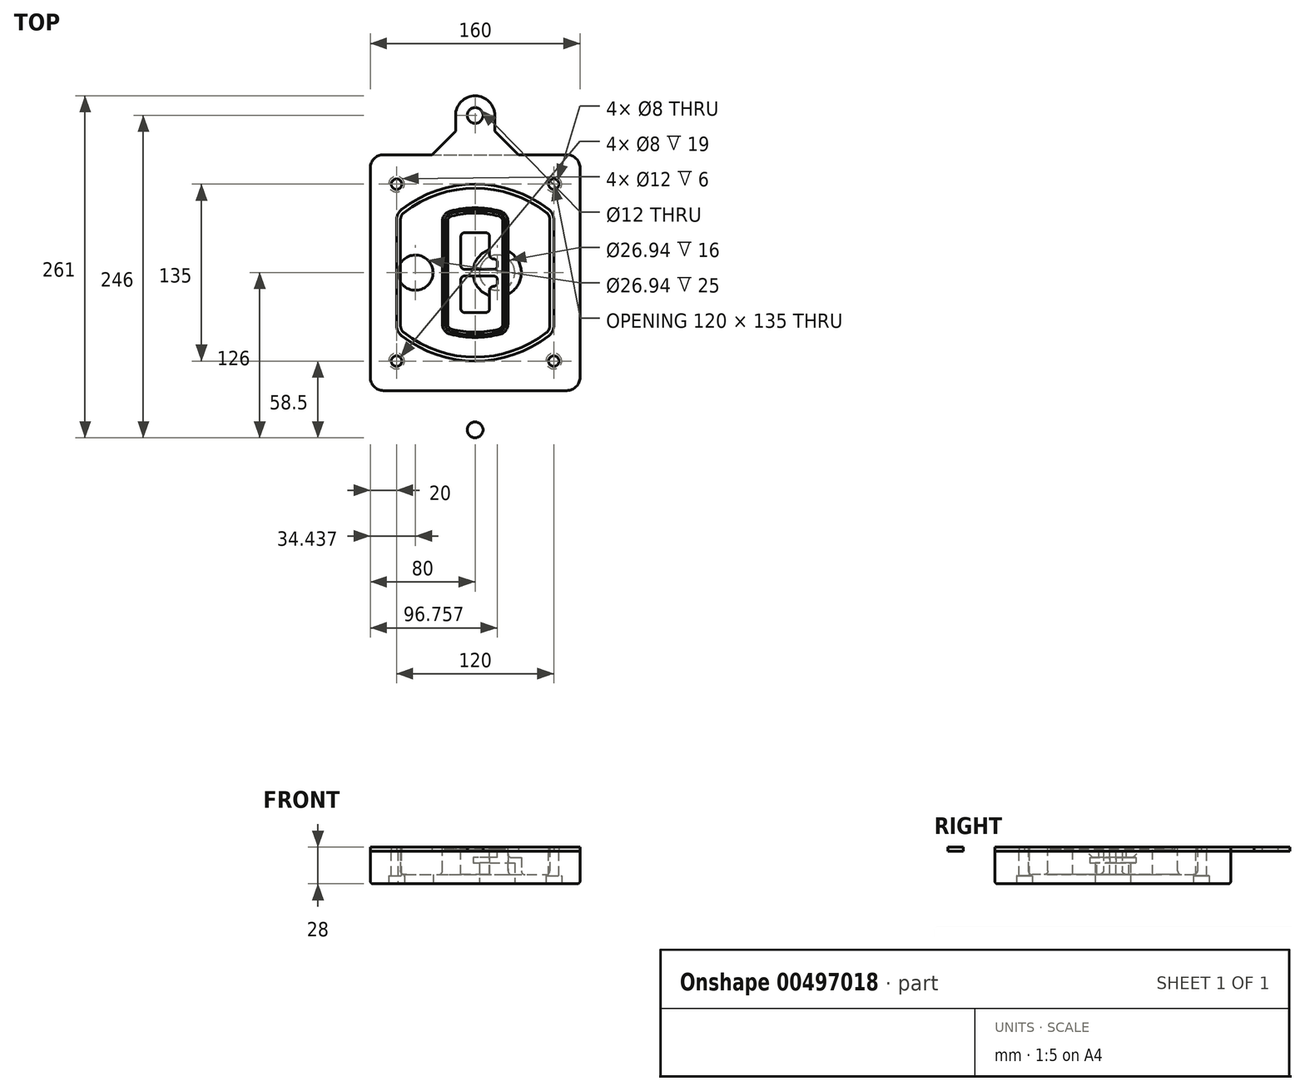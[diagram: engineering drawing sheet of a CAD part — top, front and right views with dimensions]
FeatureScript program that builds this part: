
annotation { "Feature Type Name" : "Feature", "Feature Type Description" : "" }
export const myFeature = defineFeature(function(context is Context, id is Id, definition is map)
    precondition{}
    {
        {
            var Q0;
            Q0=qCreatedBy(makeId("Top.planeOp"),FACE);
            var sketch = newSketch(context, id + "F0", { "sketchPlane" : qUnion([Q0])});
            skPoint(sketch, "E0.rect.middle", {"position": v(0, 0) * mm});
            skLineSegment(sketch, "E1.bottom", {"start": v(-70, -90) * mm, "end": v(70, -90) * mm});
            skLineSegment(sketch, "E1.top", {"start": v(-70, 90) * mm, "end": v(70, 90) * mm});
            skLineSegment(sketch, "E1.left", {"start": v(-80, -80) * mm, "end": v(-80, 80) * mm});
            skLineSegment(sketch, "E1.right", {"start": v(80, -80) * mm, "end": v(80, 80) * mm});
            skLineSegment(sketch, "E2", {"start": v(-80, 90) * mm, "end": v(80, -90) * mm, "construction": true});
            skLineSegment(sketch, "E3", {"start": v(80, 90) * mm, "end": v(-80, -90) * mm, "construction": true});
            skCircle(sketch, "E4", {"center": v(-60, 67.5) * mm, "radius": 4 * mm});
            skCircle(sketch, "E5", {"center": v(60, 67.5) * mm, "radius": 4 * mm});
            skCircle(sketch, "E6", {"center": v(60, -67.5) * mm, "radius": 4 * mm});
            skCircle(sketch, "E7", {"center": v(-60, -67.5) * mm, "radius": 4 * mm});
            skLineSegment(sketch, "E8", {"start": v(-60, 67.5) * mm, "end": v(60, 67.5) * mm, "construction": true});
            skLineSegment(sketch, "E9", {"start": v(60, 67.5) * mm, "end": v(60, -67.5) * mm, "construction": true});
            skLineSegment(sketch, "E10", {"start": v(60, -67.5) * mm, "end": v(-60, -67.5) * mm, "construction": true});
            skLineSegment(sketch, "E11", {"start": v(-60, -67.5) * mm, "end": v(-60, 67.5) * mm, "construction": true});
            skLineSegment(sketch, "E12", {"start": v(-60, 40.3) * mm, "end": v(-60, -40.3) * mm});
            skLineSegment(sketch, "E13", {"start": v(60, 40.3) * mm, "end": v(60, -40.3) * mm});
            skArc(sketch, "E14", {"start": v(56.15, 48.18) * mm, "mid": v(0, 67.5) * mm, "end": v(-56.15, 48.18) * mm});
            skArc(sketch, "E15", {"start": v(-56.15, -48.18) * mm, "mid": v(0, -67.5) * mm, "end": v(56.15, -48.18) * mm});
            skLineSegment(sketch, "E16", {"start": v(-60, 0) * mm, "end": v(60, 0) * mm, "construction": true});
            skPoint(sketch, "E17.visualSharp", {"position": v(-60, -45) * mm});
            skArc(sketch, "E17.filletArc", {"start": v(-60, -40.3) * mm, "mid": v(-58.99, -44.68) * mm, "end": v(-56.15, -48.18) * mm});
            skPoint(sketch, "E18.visualSharp", {"position": v(-60, 45) * mm});
            skArc(sketch, "E18.filletArc", {"start": v(-56.15, 48.18) * mm, "mid": v(-58.99, 44.68) * mm, "end": v(-60, 40.3) * mm});
            skPoint(sketch, "E19.visualSharp", {"position": v(60, 45) * mm});
            skArc(sketch, "E19.filletArc", {"start": v(60, 40.3) * mm, "mid": v(58.99, 44.68) * mm, "end": v(56.15, 48.18) * mm});
            skPoint(sketch, "E20.visualSharp", {"position": v(60, -45) * mm});
            skArc(sketch, "E20.filletArc", {"start": v(56.15, -48.18) * mm, "mid": v(58.99, -44.68) * mm, "end": v(60, -40.3) * mm});
            skPoint(sketch, "E21.visualSharp", {"position": v(-80, 90) * mm});
            skArc(sketch, "E21.filletArc", {"start": v(-70, 90) * mm, "mid": v(-77.07, 87.07) * mm, "end": v(-80, 80) * mm});
            skPoint(sketch, "E22.visualSharp", {"position": v(80, 90) * mm});
            skArc(sketch, "E22.filletArc", {"start": v(80, 80) * mm, "mid": v(77.07, 87.07) * mm, "end": v(70, 90) * mm});
            skPoint(sketch, "E23.visualSharp", {"position": v(80, -90) * mm});
            skArc(sketch, "E23.filletArc", {"start": v(70, -90) * mm, "mid": v(77.07, -87.07) * mm, "end": v(80, -80) * mm});
            skPoint(sketch, "E24.visualSharp", {"position": v(-80, -90) * mm});
            skArc(sketch, "E24.filletArc", {"start": v(-80, -80) * mm, "mid": v(-77.07, -87.07) * mm, "end": v(-70, -90) * mm});
            skArc(sketch, "E25.0", {"start": v(57, 40.3) * mm, "mid": v(56.3, 43.36) * mm, "end": v(54.3, 45.81) * mm});
            skLineSegment(sketch, "E25.1", {"start": v(57, 40.3) * mm, "end": v(57, -40.3) * mm});
            skArc(sketch, "E25.2", {"start": v(54.3, -45.81) * mm, "mid": v(56.3, -43.36) * mm, "end": v(57, -40.3) * mm});
            skArc(sketch, "E25.3", {"start": v(-54.3, -45.81) * mm, "mid": v(0, -64.5) * mm, "end": v(54.3, -45.81) * mm});
            skArc(sketch, "E25.4", {"start": v(-57, -40.3) * mm, "mid": v(-56.3, -43.36) * mm, "end": v(-54.3, -45.81) * mm});
            skArc(sketch, "E25.5", {"start": v(54.3, 45.81) * mm, "mid": v(0, 64.5) * mm, "end": v(-54.3, 45.81) * mm});
            skLineSegment(sketch, "E25.6", {"start": v(-57, 40.3) * mm, "end": v(-57, -40.3) * mm});
            skArc(sketch, "E25.7", {"start": v(-54.3, 45.81) * mm, "mid": v(-56.3, 43.36) * mm, "end": v(-57, 40.3) * mm});
            skArc(sketch, "E26.0", {"start": v(-58.62, 51.33) * mm, "mid": v(-62.58, 46.43) * mm, "end": v(-64, 40.3) * mm});
            skArc(sketch, "E26.1", {"start": v(58.62, 51.33) * mm, "mid": v(0, 71.5) * mm, "end": v(-58.62, 51.33) * mm});
            skArc(sketch, "E26.2", {"start": v(64, 40.3) * mm, "mid": v(62.58, 46.43) * mm, "end": v(58.62, 51.33) * mm});
            skLineSegment(sketch, "E26.3", {"start": v(64, 40.3) * mm, "end": v(64, -40.3) * mm});
            skArc(sketch, "E26.4", {"start": v(58.62, -51.33) * mm, "mid": v(62.58, -46.43) * mm, "end": v(64, -40.3) * mm});
            skLineSegment(sketch, "E26.5", {"start": v(-64, 40.3) * mm, "end": v(-64, -40.3) * mm});
            skArc(sketch, "E26.6", {"start": v(-58.62, -51.33) * mm, "mid": v(0, -71.5) * mm, "end": v(58.62, -51.33) * mm});
            skArc(sketch, "E26.7", {"start": v(-64, -40.3) * mm, "mid": v(-62.58, -46.43) * mm, "end": v(-58.62, -51.33) * mm});
            skSolve(sketch);
        }
        {
            var Q0;
            Q0=makeQuery(id+"F0.imprint","IMPRINT",FACE,{"disambiguationData":[TD([[makeQuery(id+"F0.imprint","IMPRINT",EDGE,{"derivedFrom":sQuery(id+"F0.wireOp",EDGE,"E1.bottom")}),1.0]])]});
            var Q1;
            Q1=makeQuery(id+"F0.imprint","IMPRINT",FACE,{"disambiguationData":[TD([[makeQuery(id+"F0.imprint","IMPRINT",EDGE,{"derivedFrom":sQuery(id+"F0.wireOp",EDGE,"E12")}),1.0]])]});
            var Q2;
            Q2=makeQuery(id+"F0.imprint","IMPRINT",FACE,{"disambiguationData":[TD([[makeQuery(id+"F0.imprint","IMPRINT",EDGE,{"derivedFrom":sQuery(id+"F0.wireOp",EDGE,"E25.0")}),1.0]])]});
            var Q3;
            Q3=makeQuery(id+"F0.imprint","IMPRINT",FACE,{"disambiguationData":[TD([[makeQuery(id+"F0.imprint","IMPRINT",EDGE,{"derivedFrom":sQuery(id+"F0.wireOp",EDGE,"E12")}),-1.0]])]});
            extrude(context, id + "F1", {"entities" : qUnion([Q0, Q1, Q2, Q3]), "oppositeDirection" : true, "depth" : 25 * mm});
        }
        {
            var Q0;
            Q0=makeQuery(id+"F0.imprint","IMPRINT",FACE,{"disambiguationData":[TD([[makeQuery(id+"F0.imprint","IMPRINT",EDGE,{"derivedFrom":sQuery(id+"F0.wireOp",EDGE,"E12")}),1.0]])]});
            extrude(context, id + "F2", {"entities" : qUnion([Q0]), "operationType" : NewBodyOperationType.ADD, "depth" : 3 * mm});
        }
        {
            var Q0;
            Q0=makeQuery(id+"F0.imprint","IMPRINT",FACE,{"disambiguationData":[TD([[makeQuery(id+"F0.imprint","IMPRINT",EDGE,{"derivedFrom":sQuery(id+"F0.wireOp",EDGE,"E25.0")}),1.0]])]});
            extrude(context, id + "F3", {"entities" : qUnion([Q0]), "operationType" : NewBodyOperationType.REMOVE, "oppositeDirection" : true, "depth" : 18 * mm});
        }
        {
            var Q0;
            Q0=makeQuery(id+"F2.opExtrude","CAP_FACE",FACE,{"disambiguationData":[OSD([sQuery(id+"F0.wireOp",EDGE,"E12"),sQuery(id+"F0.wireOp",EDGE,"E13"),sQuery(id+"F0.wireOp",EDGE,"E14"),sQuery(id+"F0.wireOp",EDGE,"E15"),sQuery(id+"F0.wireOp",EDGE,"E17.filletArc"),sQuery(id+"F0.wireOp",EDGE,"E18.filletArc"),sQuery(id+"F0.wireOp",EDGE,"E19.filletArc"),sQuery(id+"F0.wireOp",EDGE,"E20.filletArc"),sQuery(id+"F0.wireOp",EDGE,"E25.0"),sQuery(id+"F0.wireOp",EDGE,"E25.1"),sQuery(id+"F0.wireOp",EDGE,"E25.2"),sQuery(id+"F0.wireOp",EDGE,"E25.3"),sQuery(id+"F0.wireOp",EDGE,"E25.4"),sQuery(id+"F0.wireOp",EDGE,"E25.5"),sQuery(id+"F0.wireOp",EDGE,"E25.6"),sQuery(id+"F0.wireOp",EDGE,"E25.7")])],"isStart":false});
            var sketch = newSketch(context, id + "F4", { "sketchPlane" : qUnion([Q0])});
            skArc(sketch, "E27.0", {"start": v(-19.08, -46.97) * mm, "mid": v(0, -49.5) * mm, "end": v(19.08, -46.97) * mm});
            skArc(sketch, "E28.0", {"start": v(19.08, 46.97) * mm, "mid": v(0, 49.5) * mm, "end": v(-19.08, 46.97) * mm});
            skLineSegment(sketch, "E29", {"start": v(-25, 39.25) * mm, "end": v(-25, -39.25) * mm});
            skLineSegment(sketch, "E30", {"start": v(25, 39.25) * mm, "end": v(25, -39.25) * mm});
            skLineSegment(sketch, "E31", {"start": v(-25, 45.1) * mm, "end": v(25, 45.1) * mm, "construction": true});
            skLineSegment(sketch, "E32", {"start": v(-25, -45.1) * mm, "end": v(25, -45.1) * mm, "construction": true});
            skPoint(sketch, "E33.visualSharp", {"position": v(-25, 45.1) * mm});
            skArc(sketch, "E33.filletArc", {"start": v(-19.08, 46.97) * mm, "mid": v(-23.35, 44.11) * mm, "end": v(-25, 39.25) * mm});
            skPoint(sketch, "E34.visualSharp", {"position": v(25, 45.1) * mm});
            skArc(sketch, "E34.filletArc", {"start": v(25, 39.25) * mm, "mid": v(23.35, 44.11) * mm, "end": v(19.08, 46.97) * mm});
            skPoint(sketch, "E35.visualSharp", {"position": v(25, -45.1) * mm});
            skArc(sketch, "E35.filletArc", {"start": v(19.08, -46.97) * mm, "mid": v(23.35, -44.11) * mm, "end": v(25, -39.25) * mm});
            skPoint(sketch, "E36.visualSharp", {"position": v(-25, -45.1) * mm});
            skArc(sketch, "E36.filletArc", {"start": v(-25, -39.25) * mm, "mid": v(-23.35, -44.11) * mm, "end": v(-19.08, -46.97) * mm});
            skArc(sketch, "E37.0", {"start": v(54.3, 45.81) * mm, "mid": v(0, 64.5) * mm, "end": v(-54.3, 45.81) * mm});
            skArc(sketch, "E37.1", {"start": v(-54.3, 45.81) * mm, "mid": v(-56.3, 43.36) * mm, "end": v(-57, 40.3) * mm});
            skLineSegment(sketch, "E37.2", {"start": v(-57, 40.3) * mm, "end": v(-57, -40.3) * mm});
            skArc(sketch, "E37.3", {"start": v(-57, -40.3) * mm, "mid": v(-56.3, -43.36) * mm, "end": v(-54.3, -45.81) * mm});
            skArc(sketch, "E37.4", {"start": v(-54.3, -45.81) * mm, "mid": v(0, -64.5) * mm, "end": v(54.3, -45.81) * mm});
            skArc(sketch, "E37.5", {"start": v(54.3, -45.81) * mm, "mid": v(56.3, -43.36) * mm, "end": v(57, -40.3) * mm});
            skLineSegment(sketch, "E37.6", {"start": v(57, 40.3) * mm, "end": v(57, -40.3) * mm});
            skArc(sketch, "E37.7", {"start": v(57, 40.3) * mm, "mid": v(56.3, 43.36) * mm, "end": v(54.3, 45.81) * mm});
            skLineSegment(sketch, "E38.0", {"start": v(23, 39.25) * mm, "end": v(23, -39.25) * mm});
            skArc(sketch, "E38.1", {"start": v(18.56, -45.04) * mm, "mid": v(21.76, -42.9) * mm, "end": v(23, -39.25) * mm});
            skArc(sketch, "E38.2", {"start": v(-18.56, -45.04) * mm, "mid": v(0, -47.5) * mm, "end": v(18.56, -45.04) * mm});
            skArc(sketch, "E38.3", {"start": v(-23, -39.25) * mm, "mid": v(-21.76, -42.9) * mm, "end": v(-18.56, -45.04) * mm});
            skLineSegment(sketch, "E38.4", {"start": v(-23, 39.25) * mm, "end": v(-23, -39.25) * mm});
            skArc(sketch, "E38.5", {"start": v(23, 39.25) * mm, "mid": v(21.76, 42.9) * mm, "end": v(18.56, 45.04) * mm});
            skArc(sketch, "E38.6", {"start": v(-18.56, 45.04) * mm, "mid": v(-21.76, 42.9) * mm, "end": v(-23, 39.25) * mm});
            skArc(sketch, "E38.7", {"start": v(18.56, 45.04) * mm, "mid": v(0, 47.5) * mm, "end": v(-18.56, 45.04) * mm});
            skArc(sketch, "E39.0", {"start": v(21, 39.25) * mm, "mid": v(20.18, 41.68) * mm, "end": v(18.04, 43.1) * mm});
            skLineSegment(sketch, "E39.1", {"start": v(21, 39.25) * mm, "end": v(21, -39.25) * mm});
            skArc(sketch, "E39.2", {"start": v(18.04, -43.1) * mm, "mid": v(20.18, -41.68) * mm, "end": v(21, -39.25) * mm});
            skArc(sketch, "E39.3", {"start": v(-18.04, -43.1) * mm, "mid": v(0, -45.5) * mm, "end": v(18.04, -43.1) * mm});
            skArc(sketch, "E39.4", {"start": v(-21, -39.25) * mm, "mid": v(-20.18, -41.68) * mm, "end": v(-18.04, -43.1) * mm});
            skArc(sketch, "E39.5", {"start": v(18.04, 43.1) * mm, "mid": v(0, 45.5) * mm, "end": v(-18.04, 43.1) * mm});
            skLineSegment(sketch, "E39.6", {"start": v(-21, 39.25) * mm, "end": v(-21, -39.25) * mm});
            skArc(sketch, "E39.7", {"start": v(-18.04, 43.1) * mm, "mid": v(-20.18, 41.68) * mm, "end": v(-21, 39.25) * mm});
            skLineSegment(sketch, "E40", {"start": v(-25, 0) * mm, "end": v(25, 0) * mm, "construction": true});
            skLineSegment(sketch, "E41", {"start": v(-11, 5.5) * mm, "end": v(-11, 27.5) * mm});
            skLineSegment(sketch, "E42", {"start": v(-8, 30.5) * mm, "end": v(8, 30.5) * mm});
            skLineSegment(sketch, "E43", {"start": v(11, 27.5) * mm, "end": v(11, 13.5) * mm});
            skLineSegment(sketch, "E44", {"start": v(14, 10.5) * mm, "end": v(14, 10.5) * mm});
            skLineSegment(sketch, "E45", {"start": v(17, 7.5) * mm, "end": v(17, 5.5) * mm});
            skLineSegment(sketch, "E46", {"start": v(14, 2.5) * mm, "end": v(-8, 2.5) * mm});
            skPoint(sketch, "E47.visualSharp", {"position": v(-11, 30.5) * mm});
            skArc(sketch, "E47.filletArc", {"start": v(-8, 30.5) * mm, "mid": v(-10.12, 29.62) * mm, "end": v(-11, 27.5) * mm});
            skPoint(sketch, "E48.visualSharp", {"position": v(11, 30.5) * mm});
            skArc(sketch, "E48.filletArc", {"start": v(11, 27.5) * mm, "mid": v(10.12, 29.62) * mm, "end": v(8, 30.5) * mm});
            skPoint(sketch, "E49.visualSharp", {"position": v(11, 10.5) * mm});
            skArc(sketch, "E49.filletArc", {"start": v(11, 13.5) * mm, "mid": v(11.88, 11.38) * mm, "end": v(14, 10.5) * mm});
            skPoint(sketch, "E50.visualSharp", {"position": v(17, 10.5) * mm});
            skArc(sketch, "E50.filletArc", {"start": v(17, 7.5) * mm, "mid": v(16.12, 9.62) * mm, "end": v(14, 10.5) * mm});
            skPoint(sketch, "E51.visualSharp", {"position": v(17, 2.5) * mm});
            skArc(sketch, "E51.filletArc", {"start": v(14, 2.5) * mm, "mid": v(16.12, 3.38) * mm, "end": v(17, 5.5) * mm});
            skPoint(sketch, "E52.visualSharp", {"position": v(-11, 2.5) * mm});
            skArc(sketch, "E52.filletArc", {"start": v(-11, 5.5) * mm, "mid": v(-10.12, 3.38) * mm, "end": v(-8, 2.5) * mm});
            skLineSegment(sketch, "E53.0.MirrorCS", {"start": v(14, -2.5) * mm, "end": v(-8, -2.5) * mm});
            skArc(sketch, "E54.0.MirrorCS", {"start": v(-11, -5.5) * mm, "mid": v(-10.12, -3.38) * mm, "end": v(-8, -2.5) * mm});
            skLineSegment(sketch, "E55.0.MirrorCS", {"start": v(-11, -5.5) * mm, "end": v(-11, -27.5) * mm});
            skArc(sketch, "E56.0.MirrorCS", {"start": v(-8, -30.5) * mm, "mid": v(-10.12, -29.62) * mm, "end": v(-11, -27.5) * mm});
            skLineSegment(sketch, "E57.0.MirrorCS", {"start": v(-8, -30.5) * mm, "end": v(8, -30.5) * mm});
            skArc(sketch, "E58.0.MirrorCS", {"start": v(11, -27.5) * mm, "mid": v(10.12, -29.62) * mm, "end": v(8, -30.5) * mm});
            skLineSegment(sketch, "E59.0.MirrorCS", {"start": v(11, -27.5) * mm, "end": v(11, -13.5) * mm});
            skArc(sketch, "E60.0.MirrorCS", {"start": v(11, -13.5) * mm, "mid": v(11.88, -11.38) * mm, "end": v(14, -10.5) * mm});
            skArc(sketch, "E61.0.MirrorCS", {"start": v(17, -7.5) * mm, "mid": v(16.12, -9.62) * mm, "end": v(14, -10.5) * mm});
            skLineSegment(sketch, "E62.0.MirrorCS", {"start": v(17, -7.5) * mm, "end": v(17, -5.5) * mm});
            skArc(sketch, "E63.0.MirrorCS", {"start": v(14, -2.5) * mm, "mid": v(16.12, -3.38) * mm, "end": v(17, -5.5) * mm});
            skSolve(sketch);
        }
        {
            var Q0;
            Q0=makeQuery(id+"F4.imprint","IMPRINT",FACE,{"disambiguationData":[TD([[makeQuery(id+"F4.imprint","IMPRINT",EDGE,{"derivedFrom":sQuery(id+"F4.wireOp",EDGE,"E27.0")}),1.0]])]});
            var Q1;
            Q1=makeQuery(id+"F4.imprint","IMPRINT",FACE,{"disambiguationData":[TD([[makeQuery(id+"F4.imprint","IMPRINT",EDGE,{"derivedFrom":sQuery(id+"F4.wireOp",EDGE,"E38.0")}),-1.0]])]});
            var Q2;
            Q2=makeQuery(id+"F4.imprint","IMPRINT",FACE,{"disambiguationData":[TD([[makeQuery(id+"F4.imprint","IMPRINT",EDGE,{"derivedFrom":sQuery(id+"F4.wireOp",EDGE,"E39.0")}),1.0]])]});
            extrude(context, id + "F5", {"entities" : qUnion([Q0, Q1, Q2]), "operationType" : NewBodyOperationType.ADD, "endBound" : BoundingType.UP_TO_NEXT, "oppositeDirection" : true, "depth" : 25 * mm});
        }
        {
            var Q0;
            Q0=makeQuery(id+"F4.imprint","IMPRINT",FACE,{"disambiguationData":[TD([[makeQuery(id+"F4.imprint","IMPRINT",EDGE,{"derivedFrom":sQuery(id+"F4.wireOp",EDGE,"E38.0")}),-1.0]])]});
            extrude(context, id + "F6", {"entities" : qUnion([Q0]), "operationType" : NewBodyOperationType.REMOVE, "oppositeDirection" : true, "depth" : 2 * mm});
        }
        {
            var Q0;
            Q0=makeQuery(id+"F1.opExtrude","CAP_FACE",FACE,{"disambiguationData":[OSD([sQuery(id+"F0.wireOp",EDGE,"E1.bottom"),sQuery(id+"F0.wireOp",EDGE,"E1.top"),sQuery(id+"F0.wireOp",EDGE,"E1.left"),sQuery(id+"F0.wireOp",EDGE,"E1.right"),sQuery(id+"F0.wireOp",EDGE,"E4"),sQuery(id+"F0.wireOp",EDGE,"E5"),sQuery(id+"F0.wireOp",EDGE,"E6"),sQuery(id+"F0.wireOp",EDGE,"E7"),sQuery(id+"F0.wireOp",EDGE,"E21.filletArc"),sQuery(id+"F0.wireOp",EDGE,"E22.filletArc"),sQuery(id+"F0.wireOp",EDGE,"E23.filletArc"),sQuery(id+"F0.wireOp",EDGE,"E24.filletArc")])],"isStart":false});
            var sketch = newSketch(context, id + "F7", { "sketchPlane" : qUnion([Q0])});
            skCircle(sketch, "E64", {"center": v(16.76, 0) * mm, "radius": 13.47 * mm});
            skCircle(sketch, "E65", {"center": v(-45.56, 0) * mm, "radius": 13.47 * mm});
            skLineSegment(sketch, "E66", {"start": v(80, 0) * mm, "end": v(-80, 0) * mm});
            skCircle(sketch, "E67", {"center": v(16.76, 0) * mm, "radius": 18.47 * mm});
            skCircle(sketch, "E68", {"center": v(60, -67.5) * mm, "radius": 6 * mm});
            skCircle(sketch, "E69", {"center": v(-60, -67.5) * mm, "radius": 6 * mm});
            skCircle(sketch, "E70", {"center": v(-60, 67.5) * mm, "radius": 6 * mm});
            skCircle(sketch, "E71", {"center": v(60, 67.5) * mm, "radius": 6 * mm});
            skSolve(sketch);
        }
        {
            var Q0;
            {var subQ1=sQuery(id+"F7.wireOp",EDGE,"E66");var subQ4=sQuery(id+"F7.wireOp",EDGE,"E64");var subQ6=makeQuery(id+"F7.imprint","INTERSECT",VERTEX,{"disambiguationData":[OD(0.0)],"derivedFrom":[subQ4,subQ1]});Q0=makeQuery(id+"F7.imprint","IMPRINT",FACE,{"disambiguationData":[TD([[makeQuery(id+"F7.imprint","IMPRINT",EDGE,{"disambiguationData":[TD([[subQ6,-1.0]])],"derivedFrom":subQ4}),-1.0]])]});}
            var Q1;
            {var subQ0=sQuery(id+"F7.wireOp",EDGE,"E66");var subQ1=sQuery(id+"F7.wireOp",EDGE,"E64");var subQ3=makeQuery(id+"F7.imprint","INTERSECT",VERTEX,{"disambiguationData":[OD(0.0)],"derivedFrom":[subQ1,subQ0]});Q1=makeQuery(id+"F7.imprint","IMPRINT",FACE,{"disambiguationData":[TD([[makeQuery(id+"F7.imprint","IMPRINT",EDGE,{"disambiguationData":[TD([[subQ3,-1.0]])],"derivedFrom":subQ1}),1.0]])]});}
            var Q2;
            {var subQ0=sQuery(id+"F7.wireOp",EDGE,"E66");var subQ1=sQuery(id+"F7.wireOp",EDGE,"E64");var subQ3=makeQuery(id+"F7.imprint","INTERSECT",VERTEX,{"disambiguationData":[OD(0.0)],"derivedFrom":[subQ1,subQ0]});Q2=makeQuery(id+"F7.imprint","IMPRINT",FACE,{"disambiguationData":[TD([[makeQuery(id+"F7.imprint","IMPRINT",EDGE,{"disambiguationData":[TD([[subQ3,1.0]])],"derivedFrom":subQ1}),1.0]])]});}
            var Q3;
            {var subQ1=sQuery(id+"F7.wireOp",EDGE,"E66");var subQ4=sQuery(id+"F7.wireOp",EDGE,"E64");var subQ6=makeQuery(id+"F7.imprint","INTERSECT",VERTEX,{"disambiguationData":[OD(0.0)],"derivedFrom":[subQ4,subQ1]});Q3=makeQuery(id+"F7.imprint","IMPRINT",FACE,{"disambiguationData":[TD([[makeQuery(id+"F7.imprint","IMPRINT",EDGE,{"disambiguationData":[TD([[subQ6,1.0]])],"derivedFrom":subQ4}),-1.0]])]});}
            extrude(context, id + "F8", {"entities" : qUnion([Q0, Q1, Q2, Q3]), "operationType" : NewBodyOperationType.ADD, "oppositeDirection" : true, "depth" : 20 * mm});
        }
        {
            var Q0;
            {var subQ0=sQuery(id+"F7.wireOp",EDGE,"E66");var subQ1=sQuery(id+"F7.wireOp",EDGE,"E64");var subQ3=makeQuery(id+"F7.imprint","INTERSECT",VERTEX,{"disambiguationData":[OD(0.0)],"derivedFrom":[subQ1,subQ0]});Q0=makeQuery(id+"F7.imprint","IMPRINT",FACE,{"disambiguationData":[TD([[makeQuery(id+"F7.imprint","IMPRINT",EDGE,{"disambiguationData":[TD([[subQ3,-1.0]])],"derivedFrom":subQ1}),1.0]])]});}
            var Q1;
            {var subQ0=sQuery(id+"F7.wireOp",EDGE,"E66");var subQ1=sQuery(id+"F7.wireOp",EDGE,"E64");var subQ3=makeQuery(id+"F7.imprint","INTERSECT",VERTEX,{"disambiguationData":[OD(0.0)],"derivedFrom":[subQ1,subQ0]});Q1=makeQuery(id+"F7.imprint","IMPRINT",FACE,{"disambiguationData":[TD([[makeQuery(id+"F7.imprint","IMPRINT",EDGE,{"disambiguationData":[TD([[subQ3,1.0]])],"derivedFrom":subQ1}),1.0]])]});}
            extrude(context, id + "F9", {"entities" : qUnion([Q0, Q1]), "operationType" : NewBodyOperationType.REMOVE, "oppositeDirection" : true, "depth" : 16 * mm});
        }
        {
            var Q0;
            {var subQ0=sQuery(id+"F7.wireOp",EDGE,"E66");var subQ1=sQuery(id+"F7.wireOp",EDGE,"E65");var subQ3=makeQuery(id+"F7.imprint","INTERSECT",VERTEX,{"disambiguationData":[OD(0.0)],"derivedFrom":[subQ1,subQ0]});Q0=makeQuery(id+"F7.imprint","IMPRINT",FACE,{"disambiguationData":[TD([[makeQuery(id+"F7.imprint","IMPRINT",EDGE,{"disambiguationData":[TD([[subQ3,-1.0]])],"derivedFrom":subQ1}),1.0]])]});}
            var Q1;
            {var subQ0=sQuery(id+"F7.wireOp",EDGE,"E66");var subQ1=sQuery(id+"F7.wireOp",EDGE,"E65");var subQ3=makeQuery(id+"F7.imprint","INTERSECT",VERTEX,{"disambiguationData":[OD(0.0)],"derivedFrom":[subQ1,subQ0]});Q1=makeQuery(id+"F7.imprint","IMPRINT",FACE,{"disambiguationData":[TD([[makeQuery(id+"F7.imprint","IMPRINT",EDGE,{"disambiguationData":[TD([[subQ3,1.0]])],"derivedFrom":subQ1}),1.0]])]});}
            extrude(context, id + "F10", {"entities" : qUnion([Q0, Q1]), "operationType" : NewBodyOperationType.REMOVE, "oppositeDirection" : true, "depth" : 25 * mm});
        }
        {
            var Q0;
            Q0=makeQuery(id+"F7.imprint","IMPRINT",FACE,{"disambiguationData":[TD([[makeQuery(id+"F7.imprint","IMPRINT",EDGE,{"derivedFrom":sQuery(id+"F7.wireOp",EDGE,"E68")}),1.0]])]});
            var Q1;
            Q1=makeQuery(id+"F7.imprint","IMPRINT",FACE,{"disambiguationData":[TD([[makeQuery(id+"F7.imprint","IMPRINT",EDGE,{"derivedFrom":makeQuery(id+"F1.opExtrude","CAP_EDGE",EDGE,{"disambiguationData":[OSD([sQuery(id+"F0.wireOp",EDGE,"E5")])],"isStart":false})}),-1.0]])]});
            var Q2;
            Q2=makeQuery(id+"F7.imprint","IMPRINT",FACE,{"disambiguationData":[TD([[makeQuery(id+"F7.imprint","IMPRINT",EDGE,{"derivedFrom":sQuery(id+"F7.wireOp",EDGE,"E69")}),1.0]])]});
            var Q3;
            Q3=makeQuery(id+"F7.imprint","IMPRINT",FACE,{"disambiguationData":[TD([[makeQuery(id+"F7.imprint","IMPRINT",EDGE,{"derivedFrom":makeQuery(id+"F1.opExtrude","CAP_EDGE",EDGE,{"disambiguationData":[OSD([sQuery(id+"F0.wireOp",EDGE,"E4")])],"isStart":false})}),-1.0]])]});
            var Q4;
            Q4=makeQuery(id+"F7.imprint","IMPRINT",FACE,{"disambiguationData":[TD([[makeQuery(id+"F7.imprint","IMPRINT",EDGE,{"derivedFrom":sQuery(id+"F7.wireOp",EDGE,"E70")}),1.0]])]});
            var Q5;
            Q5=makeQuery(id+"F7.imprint","IMPRINT",FACE,{"disambiguationData":[TD([[makeQuery(id+"F7.imprint","IMPRINT",EDGE,{"derivedFrom":makeQuery(id+"F1.opExtrude","CAP_EDGE",EDGE,{"disambiguationData":[OSD([sQuery(id+"F0.wireOp",EDGE,"E7")])],"isStart":false})}),-1.0]])]});
            var Q6;
            Q6=makeQuery(id+"F7.imprint","IMPRINT",FACE,{"disambiguationData":[TD([[makeQuery(id+"F7.imprint","IMPRINT",EDGE,{"derivedFrom":sQuery(id+"F7.wireOp",EDGE,"E71")}),1.0]])]});
            var Q7;
            Q7=makeQuery(id+"F7.imprint","IMPRINT",FACE,{"disambiguationData":[TD([[makeQuery(id+"F7.imprint","IMPRINT",EDGE,{"derivedFrom":makeQuery(id+"F1.opExtrude","CAP_EDGE",EDGE,{"disambiguationData":[OSD([sQuery(id+"F0.wireOp",EDGE,"E6")])],"isStart":false})}),-1.0]])]});
            extrude(context, id + "F11", {"entities" : qUnion([Q0, Q1, Q2, Q3, Q4, Q5, Q6, Q7]), "operationType" : NewBodyOperationType.REMOVE, "oppositeDirection" : true, "depth" : 6 * mm});
        }
        {
            var Q0;
            Q0=makeQuery(id+"F9.boolean.opBoolean","COPY",FACE,{"derivedFrom":makeQuery(id+"F9.opExtrude","CAP_FACE",FACE,{"disambiguationData":[OSD([sQuery(id+"F7.wireOp",EDGE,"E64")])],"isStart":false})});
            var sketch = newSketch(context, id + "F12", { "sketchPlane" : qUnion([Q0])});
            skArc(sketch, "E72.0", {"start": v(11, 17.55) * mm, "mid": v(2.57, 11.82) * mm, "end": v(-1.54, 2.5) * mm});
            skArc(sketch, "E72.1", {"start": v(-1.54, -2.5) * mm, "mid": v(2.57, -11.82) * mm, "end": v(11, -17.55) * mm});
            skLineSegment(sketch, "E73", {"start": v(-1.54, -2.5) * mm, "end": v(14, -2.5) * mm});
            skLineSegment(sketch, "E74.0", {"start": v(14, 2.5) * mm, "end": v(-1.54, 2.5) * mm});
            skArc(sketch, "E74.1", {"start": v(14, 2.5) * mm, "mid": v(16.12, 3.38) * mm, "end": v(17, 5.5) * mm});
            skLineSegment(sketch, "E74.2", {"start": v(17, 7.5) * mm, "end": v(17, 5.5) * mm});
            skArc(sketch, "E74.3", {"start": v(17, 7.5) * mm, "mid": v(16.12, 9.62) * mm, "end": v(14, 10.5) * mm});
            skArc(sketch, "E74.4", {"start": v(11, 13.5) * mm, "mid": v(11.88, 11.38) * mm, "end": v(14, 10.5) * mm});
            skLineSegment(sketch, "E74.5", {"start": v(11, 17.55) * mm, "end": v(11, 13.5) * mm});
            skLineSegment(sketch, "E74.7", {"start": v(14, -2.5) * mm, "end": v(-1.54, -2.5) * mm});
            skArc(sketch, "E74.8", {"start": v(14, -2.5) * mm, "mid": v(16.12, -3.38) * mm, "end": v(17, -5.5) * mm});
            skLineSegment(sketch, "E74.9", {"start": v(17, -7.5) * mm, "end": v(17, -5.5) * mm});
            skArc(sketch, "E74.10", {"start": v(17, -7.5) * mm, "mid": v(16.12, -9.62) * mm, "end": v(14, -10.5) * mm});
            skArc(sketch, "E74.11", {"start": v(11, -13.5) * mm, "mid": v(11.88, -11.38) * mm, "end": v(14, -10.5) * mm});
            skLineSegment(sketch, "E74.12", {"start": v(11, -17.55) * mm, "end": v(11, -13.5) * mm});
            skPoint(sketch, "E75.orphan", {"position": v(11, -27.5) * mm});
            skPoint(sketch, "E76.orphan", {"position": v(-8, -2.5) * mm});
            skPoint(sketch, "E77.orphan", {"position": v(-8, 2.5) * mm});
            skPoint(sketch, "E78.orphan", {"position": v(11, 27.5) * mm});
            skSolve(sketch);
        }
        {
            var Q0;
            {var subQ7=sQuery(id+"F12.wireOp",EDGE,"E72.0");var subQ14=sQuery(id+"F12.wireOp",EDGE,"E72.1");var subQ16=sQuery(id+"F12.wireOp",EDGE,"E74.1");var subQ18=sQuery(id+"F12.wireOp",EDGE,"E74.8");Q0=qUnion([makeQuery(id+"F12.imprint","IMPRINT",FACE,{"disambiguationData":[TD([[makeQuery(id+"F12.imprint","IMPRINT",EDGE,{"derivedFrom":subQ7}),1.0]])]}),makeQuery(id+"F12.imprint","IMPRINT",FACE,{"disambiguationData":[TD([[makeQuery(id+"F12.imprint","IMPRINT",EDGE,{"derivedFrom":subQ14}),1.0]])]}),makeQuery(id+"F12.imprint","IMPRINT",FACE,{"disambiguationData":[TD([[makeQuery(id+"F12.imprint","IMPRINT",EDGE,{"derivedFrom":subQ16}),1.0]])]}),makeQuery(id+"F12.imprint","IMPRINT",FACE,{"disambiguationData":[TD([[makeQuery(id+"F12.imprint","IMPRINT",EDGE,{"derivedFrom":subQ18}),-1.0]])]})]);}
            var Q1;
            Q1=makeQuery(id+"F5.boolean.opBoolean","SPLIT",FACE,{"disambiguationData":[TD([makeQuery(id+"F5.opExtrude","SWEPT_FACE",FACE,{"disambiguationData":[OSD([sQuery(id+"F4.wireOp",EDGE,"E41")])]})])],"derivedFrom":makeQuery(id+"F3.boolean.opBoolean","COPY",FACE,{"derivedFrom":makeQuery(id+"F3.opExtrude","CAP_FACE",FACE,{"disambiguationData":[OSD([sQuery(id+"F0.wireOp",EDGE,"E25.0"),sQuery(id+"F0.wireOp",EDGE,"E25.1"),sQuery(id+"F0.wireOp",EDGE,"E25.2"),sQuery(id+"F0.wireOp",EDGE,"E25.3"),sQuery(id+"F0.wireOp",EDGE,"E25.4"),sQuery(id+"F0.wireOp",EDGE,"E25.5"),sQuery(id+"F0.wireOp",EDGE,"E25.6"),sQuery(id+"F0.wireOp",EDGE,"E25.7")])],"isStart":false})})});
            extrude(context, id + "F13", {"entities" : qUnion([Q0]), "operationType" : NewBodyOperationType.REMOVE, "endBound" : BoundingType.UP_TO_SURFACE, "endBoundEntityFace" : qUnion([Q1]), "depth" : 25 * mm});
        }
        {
            var Q0;
            Q0=makeQuery(id+"F3.boolean.opBoolean","COPY",EDGE,{"derivedFrom":makeQuery(id+"F3.opExtrude","CAP_EDGE",EDGE,{"disambiguationData":[OSD([sQuery(id+"F0.wireOp",EDGE,"E25.6")])],"isStart":false})});
            var Q1;
            Q1=makeQuery(id+"F8.boolean.opBoolean","INTERSECT",EDGE,{"derivedFrom":[makeQuery(id+"F5.opExtrude","SWEPT_FACE",FACE,{"disambiguationData":[OSD([sQuery(id+"F4.wireOp",EDGE,"E30")])]}),makeQuery(id+"F8.opExtrude","CAP_FACE",FACE,{"disambiguationData":[OSD([sQuery(id+"F7.wireOp",EDGE,"E67")])],"isStart":false})]});
            var Q2;
            Q2=makeQuery(id+"F8.boolean.opBoolean","INTERSECT",EDGE,{"disambiguationData":[OD(1.0)],"derivedFrom":[makeQuery(id+"F5.opExtrude","SWEPT_FACE",FACE,{"disambiguationData":[OSD([sQuery(id+"F4.wireOp",EDGE,"E30")])]}),makeQuery(id+"F8.opExtrude","SWEPT_FACE",FACE,{"disambiguationData":[OSD([sQuery(id+"F7.wireOp",EDGE,"E67")])]})]});
            var Q3;
            {var subQ0=sQuery(id+"F4.wireOp",EDGE,"E30");Q3=makeQuery(id+"F8.boolean.opBoolean","SPLIT",EDGE,{"disambiguationData":[TD([makeQuery(id+"F5.opExtrude","SWEPT_FACE",FACE,{"disambiguationData":[OSD([sQuery(id+"F4.wireOp",EDGE,"E35.filletArc")])]})])],"derivedFrom":makeQuery(id+"F5.opExtrude","CAP_EDGE",EDGE,{"disambiguationData":[OSD([subQ0])],"isStart":false})});}
            var Q4;
            {var subQ0=sQuery(id+"F0.wireOp",EDGE,"E25.7");var subQ1=sQuery(id+"F0.wireOp",EDGE,"E25.1");var subQ2=sQuery(id+"F0.wireOp",EDGE,"E25.6");var subQ3=sQuery(id+"F0.wireOp",EDGE,"E25.5");var subQ4=sQuery(id+"F0.wireOp",EDGE,"E25.4");var subQ5=sQuery(id+"F0.wireOp",EDGE,"E25.0");var subQ6=sQuery(id+"F0.wireOp",EDGE,"E25.2");var subQ7=sQuery(id+"F0.wireOp",EDGE,"E25.3");Q4=makeQuery(id+"F8.boolean.opBoolean","INTERSECT",EDGE,{"derivedFrom":[makeQuery(id+"F5.boolean.opBoolean","SPLIT",FACE,{"disambiguationData":[TD([makeQuery(id+"F2.opExtrude","SWEPT_FACE",FACE,{"disambiguationData":[OSD([subQ5])]})])],"derivedFrom":makeQuery(id+"F3.boolean.opBoolean","COPY",FACE,{"derivedFrom":makeQuery(id+"F3.opExtrude","CAP_FACE",FACE,{"disambiguationData":[OSD([subQ5,subQ1,subQ6,subQ7,subQ4,subQ3,subQ2,subQ0])],"isStart":false})})}),makeQuery(id+"F8.opExtrude","SWEPT_FACE",FACE,{"disambiguationData":[OSD([sQuery(id+"F7.wireOp",EDGE,"E67")])]})]});}
            var Q5;
            Q5=makeQuery(id+"F8.boolean.opBoolean","INTERSECT",EDGE,{"disambiguationData":[OD(0.0)],"derivedFrom":[makeQuery(id+"F5.opExtrude","SWEPT_FACE",FACE,{"disambiguationData":[OSD([sQuery(id+"F4.wireOp",EDGE,"E30")])]}),makeQuery(id+"F8.opExtrude","SWEPT_FACE",FACE,{"disambiguationData":[OSD([sQuery(id+"F7.wireOp",EDGE,"E67")])]})]});
            fillet(context, id + "F14", {"entities" : qUnion([Q0, Q1, Q2, Q3, Q4, Q5]), "radius" : 3 * mm, "tangentPropagation" : true, "allowEdgeOverflow" : false});
        }
        {
            var Q0;
            Q0=makeQuery(id+"F1.opExtrude","CAP_EDGE",EDGE,{"disambiguationData":[OSD([sQuery(id+"F0.wireOp",EDGE,"E1.bottom")])],"isStart":false});
            fillet(context, id + "F15", {"entities" : qUnion([Q0]), "radius" : 2 * mm, "tangentPropagation" : true, "allowEdgeOverflow" : false});
        }
        {
            var Q0;
            {var subQ0=sQuery(id+"F0.wireOp",EDGE,"E21.filletArc");var subQ1=sQuery(id+"F0.wireOp",EDGE,"E7");var subQ2=sQuery(id+"F0.wireOp",EDGE,"E6");var subQ3=sQuery(id+"F0.wireOp",EDGE,"E5");var subQ4=sQuery(id+"F0.wireOp",EDGE,"E4");var subQ5=sQuery(id+"F0.wireOp",EDGE,"E22.filletArc");var subQ6=sQuery(id+"F0.wireOp",EDGE,"E1.bottom");var subQ7=sQuery(id+"F0.wireOp",EDGE,"E1.right");var subQ8=sQuery(id+"F0.wireOp",EDGE,"E1.top");var subQ9=sQuery(id+"F0.wireOp",EDGE,"E1.left");var subQ10=sQuery(id+"F0.wireOp",EDGE,"E23.filletArc");var subQ11=sQuery(id+"F0.wireOp",EDGE,"E24.filletArc");Q0=makeQuery(id+"F2.boolean.opBoolean","SPLIT",FACE,{"disambiguationData":[TD([makeQuery(id+"F1.opExtrude","SWEPT_FACE",FACE,{"disambiguationData":[OSD([subQ6])]})])],"derivedFrom":makeQuery(id+"F1.opExtrude","CAP_FACE",FACE,{"disambiguationData":[OSD([subQ6,subQ8,subQ9,subQ7,subQ4,subQ3,subQ2,subQ1,subQ0,subQ5,subQ10,subQ11])],"isStart":true})});}
            var sketch = newSketch(context, id + "F16", { "sketchPlane" : qUnion([Q0])});
            skLineSegment(sketch, "E79", {"start": v(-33, 90) * mm, "end": v(-15, 108) * mm});
            skLineSegment(sketch, "E80", {"start": v(-15, 108) * mm, "end": v(-15, 120) * mm});
            skLineSegment(sketch, "E81", {"start": v(33, 90) * mm, "end": v(15, 108) * mm});
            skLineSegment(sketch, "E82", {"start": v(15, 108) * mm, "end": v(15, 120) * mm});
            skArc(sketch, "E83", {"start": v(15, 120) * mm, "mid": v(0, 135) * mm, "end": v(-15, 120) * mm});
            skCircle(sketch, "E84", {"center": v(0, 120) * mm, "radius": 6 * mm});
            skLineSegment(sketch, "E85", {"start": v(0, 120) * mm, "end": v(0, 90) * mm, "construction": true});
            skLineSegment(sketch, "E86", {"start": v(0, 0) * mm, "end": v(80, 0) * mm, "construction": true});
            skLineSegment(sketch, "E87", {"start": v(80, 0) * mm, "end": v(-80, 0) * mm, "construction": true});
            skLineSegment(sketch, "E88.MirrorCS", {"start": v(15, -108) * mm, "end": v(15, -120) * mm});
            skLineSegment(sketch, "E89.MirrorCS", {"start": v(-15, -108) * mm, "end": v(-15, -120) * mm});
            skCircle(sketch, "E90.MirrorC", {"center": v(0, -120) * mm, "radius": 6 * mm});
            skArc(sketch, "E91.MirrorCS", {"start": v(15, -120) * mm, "mid": v(0, -135) * mm, "end": v(-15, -120) * mm});
            skLineSegment(sketch, "E92.MirrorCS", {"start": v(33, -90) * mm, "end": v(15, -108) * mm});
            skLineSegment(sketch, "E93.MirrorCS", {"start": v(-33, -90) * mm, "end": v(-15, -108) * mm});
            skLineSegment(sketch, "E94.MirrorCS", {"start": v(0, -120) * mm, "end": v(0, -90) * mm, "construction": true});
            skSolve(sketch);
        }
        {
            var Q0;
            {var subQ1=sQuery(id+"F16.wireOp",EDGE,"E79");Q0=makeQuery(id+"F16.imprint","IMPRINT",FACE,{"disambiguationData":[TD([[makeQuery(id+"F16.imprint","IMPRINT",EDGE,{"derivedFrom":subQ1}),-1.0]])]});}
            var Q1;
            Q1=makeQuery(id+"F16.imprint","IMPRINT",FACE,{"disambiguationData":[TD([[makeQuery(id+"F16.imprint","IMPRINT",EDGE,{"derivedFrom":makeQuery(id+"F1.opExtrude","CAP_EDGE",EDGE,{"disambiguationData":[OSD([sQuery(id+"F0.wireOp",EDGE,"E1.left")])],"isStart":true})}),-1.0]])]});
            var Q2;
            Q2=makeQuery(id+"F16.imprint","IMPRINT",FACE,{"disambiguationData":[TD([[makeQuery(id+"F16.imprint","IMPRINT",EDGE,{"derivedFrom":sQuery(id+"F16.wireOp",EDGE,"E90.MirrorC")}),1.0]])]});
            var Q3;
            Q3=makeQuery(id+"F2.opExtrude","CAP_FACE",FACE,{"disambiguationData":[OSD([sQuery(id+"F0.wireOp",EDGE,"E12"),sQuery(id+"F0.wireOp",EDGE,"E13"),sQuery(id+"F0.wireOp",EDGE,"E14"),sQuery(id+"F0.wireOp",EDGE,"E15"),sQuery(id+"F0.wireOp",EDGE,"E17.filletArc"),sQuery(id+"F0.wireOp",EDGE,"E18.filletArc"),sQuery(id+"F0.wireOp",EDGE,"E19.filletArc"),sQuery(id+"F0.wireOp",EDGE,"E20.filletArc"),sQuery(id+"F0.wireOp",EDGE,"E25.0"),sQuery(id+"F0.wireOp",EDGE,"E25.1"),sQuery(id+"F0.wireOp",EDGE,"E25.2"),sQuery(id+"F0.wireOp",EDGE,"E25.3"),sQuery(id+"F0.wireOp",EDGE,"E25.4"),sQuery(id+"F0.wireOp",EDGE,"E25.5"),sQuery(id+"F0.wireOp",EDGE,"E25.6"),sQuery(id+"F0.wireOp",EDGE,"E25.7")])],"isStart":false});
            extrude(context, id + "F17", {"entities" : qUnion([Q0, Q1, Q2]), "endBound" : BoundingType.UP_TO_SURFACE, "endBoundEntityFace" : qUnion([Q3]), "depth" : 5 * mm});
        }
    });
